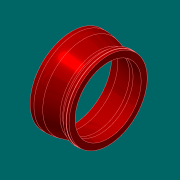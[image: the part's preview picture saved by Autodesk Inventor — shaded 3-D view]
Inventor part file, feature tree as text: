
AUTODESK INVENTOR PART (.ipt)
format: ipt  version: 2017.3 (Build 213257000, 257)  size: 232,960 bytes
history: native  units: in
note: dims shown in document units (in); Inventor stores cm internally (conversion verified against a paired STEP export)
features: sketch x4, extrude x3, fillet x2, revolve x1, chamfer x1
ambient origin geometry x8: Origin, YZ Plane, XZ Plane, XY Plane, X Axis, Y Axis, Z Axis, Center Point
bodies: Solid1 (feature_tree)
feature tree (11):
  revolve  "Revolution1"  [1 undecoded]
  extrude  "Extrusion1"  Depth=24.5in
  extrude  "Extrusion2"  Depth=6.0in
  extrude  "Extrusion3"  Depth=12.0in
  fillet  "Fillet1"  Radius=1.5in
  chamfer  "Chamfer1"  Distance=1.25in
  fillet  "Fillet2"  Radius=3.0in
  sketch  "Sketch1"  dims[d0=13.4528in d1=28.5in]
  sketch  "Sketch2"  dims[d2=1.25in d3=24.5in]
  sketch  "Sketch3"  dims[d4=12.0in d5=6.0in]
  sketch  "Sketch4"  dims[d6=12.0in d7=12.0in d8=1.5in d9=1.25in d10=3.0in d12=0.0964in d13=90.0deg d14=30.0in d15=0.5in d16=0.0in d17=29.25in d18=2.0in d19=0.0in d20=0.0312in d21=0.0312in d22=0.125in d23=45.0deg d27=28.98in d28=1.0in d29=0.0in d30=1.0in]
note: 1 required parameter value undecoded (feature->parameter linkage not recoverable at this tier; creation-order binding heuristic only, values carry confidence <= 0.55)
